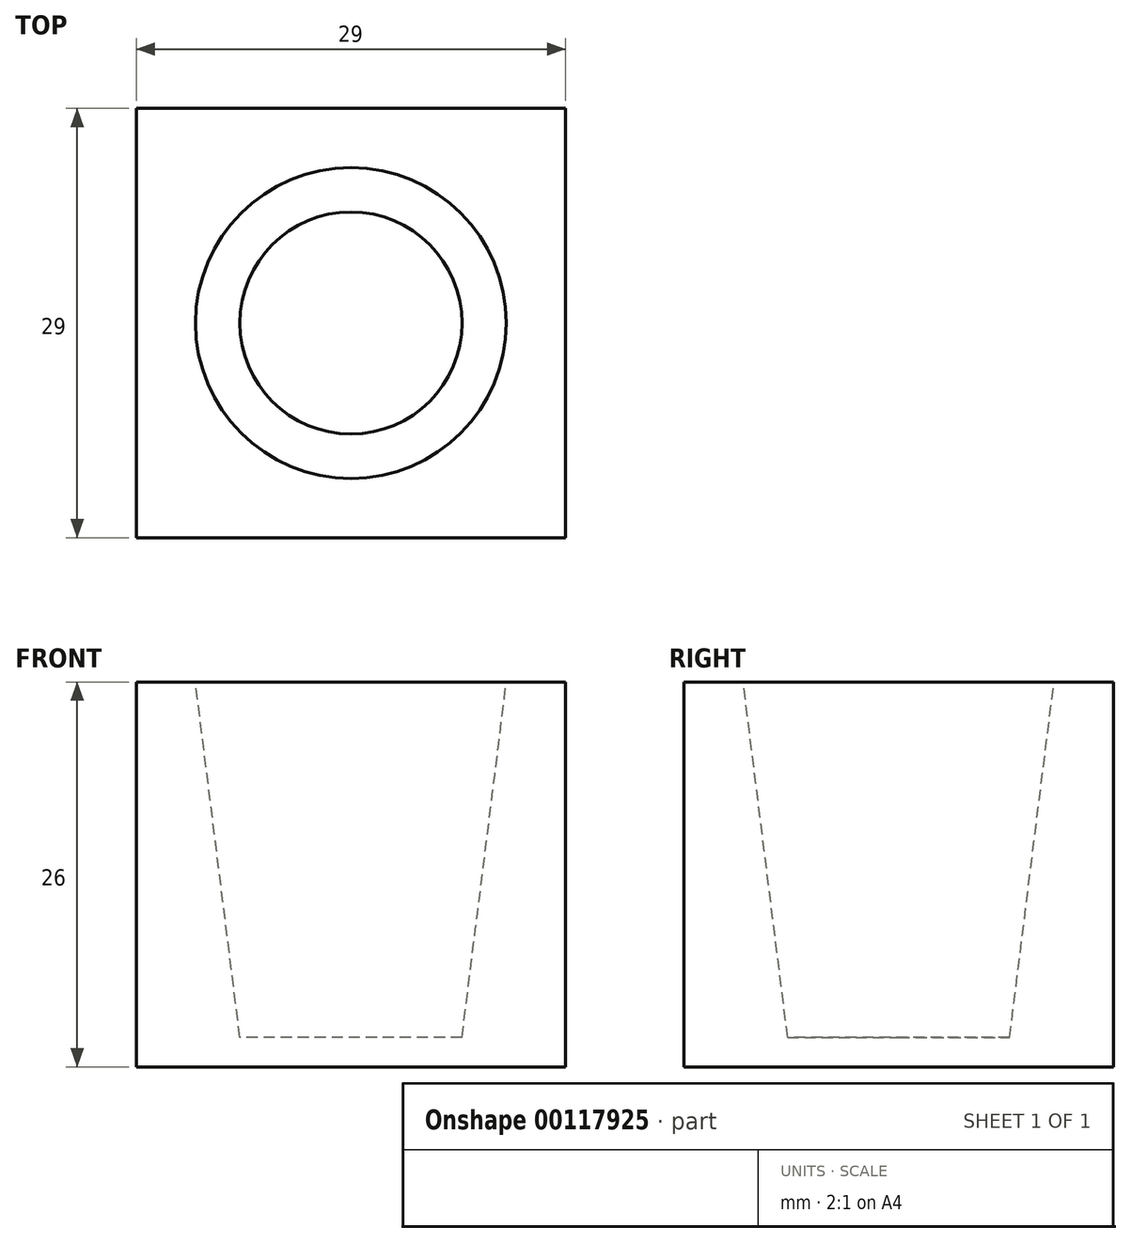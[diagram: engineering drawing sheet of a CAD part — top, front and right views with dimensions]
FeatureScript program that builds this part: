
annotation { "Feature Type Name" : "Feature", "Feature Type Description" : "" }
export const myFeature = defineFeature(function(context is Context, id is Id, definition is map)
    precondition{}
    {
        {
            var Q0;
            Q0=qCreatedBy(makeId("Top.planeOp"),FACE);
            var sketch = newSketch(context, id + "F0", { "sketchPlane" : qUnion([Q0])});
            skCircle(sketch, "E0", {"center": v(0, 0) * mm, "radius": 7.5 * mm});
            skCircle(sketch, "E1", {"center": v(0, 0) * mm, "radius": 10.5 * mm});
            skLineSegment(sketch, "E2.bottom", {"start": v(14.5, -14.5) * mm, "end": v(-14.5, -14.5) * mm});
            skLineSegment(sketch, "E2.top", {"start": v(14.5, 14.5) * mm, "end": v(-14.5, 14.5) * mm});
            skLineSegment(sketch, "E2.left", {"start": v(14.5, -14.5) * mm, "end": v(14.5, 14.5) * mm});
            skLineSegment(sketch, "E2.right", {"start": v(-14.5, -14.5) * mm, "end": v(-14.5, 14.5) * mm});
            skSolve(sketch);
        }
        {
            var Q0;
            Q0=qCreatedBy(makeId("Top.planeOp"),FACE);
            cPlane(context, id + "F1", {"entities" : qUnion([Q0]), "cplaneType" : CPlaneType.OFFSET, "offset" : 24 * mm, "width" : 150 * mm, "height" : 150 * mm});
        }
        {
            var Q0;
            Q0=qCreatedBy(id+"F1.planeOp",FACE);
            var sketch = newSketch(context, id + "F2", { "sketchPlane" : qUnion([Q0])});
            skCircle(sketch, "E3.0", {"center": v(0, 0) * mm, "radius": 10.5 * mm});
            skSolve(sketch);
        }
        {
            var Q0;
            Q0=makeQuery(id+"F0.imprint","IMPRINT",FACE,{"disambiguationData":[TD([[makeQuery(id+"F0.imprint","IMPRINT",EDGE,{"derivedFrom":sQuery(id+"F0.wireOp",EDGE,"E1")}),-1.0]])]});
            var Q1;
            Q1=makeQuery(id+"F0.imprint","IMPRINT",FACE,{"disambiguationData":[TD([[makeQuery(id+"F0.imprint","IMPRINT",EDGE,{"derivedFrom":sQuery(id+"F0.wireOp",EDGE,"E0")}),-1.0]])]});
            var Q2;
            Q2=qCreatedBy(id+"F1.planeOp",FACE);
            extrude(context, id + "F3", {"entities" : qUnion([Q0, Q1]), "endBound" : BoundingType.UP_TO_SURFACE, "endBoundEntityFace" : qUnion([Q2]), "depth" : 25 * mm});
        }
        {
            var Q1;
            Q1=makeQuery(id+"F0.imprint","IMPRINT",FACE,{"disambiguationData":[TD([[makeQuery(id+"F0.imprint","IMPRINT",EDGE,{"derivedFrom":sQuery(id+"F0.wireOp",EDGE,"E0")}),1.0]])]});
            var Q2;
            Q2=makeQuery(id+"F2.imprint","IMPRINT",FACE,{"disambiguationData":[TD([[makeQuery(id+"F2.imprint","IMPRINT",EDGE,{"derivedFrom":sQuery(id+"F2.wireOp",EDGE,"E3.0")}),1.0]])]});
            var Q3;
            Q3=sQuery(id+"F2.wireOp",EDGE,"E3.0");
            var Q4;
            Q4=sQuery(id+"F0.wireOp",EDGE,"E0");
            loft(context, id + "F4", {"operationType" : NewBodyOperationType.REMOVE, "sheetProfilesArray" : [{ "sheetProfileEntities" : qUnion([Q1]) }, { "sheetProfileEntities" : qUnion([Q2]) }], "wireProfilesArray" : [{ "wireProfileEntities" : qUnion([Q3]) }, { "wireProfileEntities" : qUnion([Q4]) }]});
        }
        {
            var Q0;
            Q0=makeQuery(id+"F0.imprint","IMPRINT",FACE,{"disambiguationData":[TD([[makeQuery(id+"F0.imprint","IMPRINT",EDGE,{"derivedFrom":sQuery(id+"F0.wireOp",EDGE,"E1")}),-1.0]])]});
            var Q1;
            Q1=makeQuery(id+"F0.imprint","IMPRINT",FACE,{"disambiguationData":[TD([[makeQuery(id+"F0.imprint","IMPRINT",EDGE,{"derivedFrom":sQuery(id+"F0.wireOp",EDGE,"E0")}),-1.0]])]});
            extrude(context, id + "F5", {"entities" : qUnion([Q0, Q1]), "operationType" : NewBodyOperationType.ADD, "oppositeDirection" : true, "depth" : 1 * mm});
        }
        {
            var Q0;
            Q0=makeQuery(id+"F0.imprint","IMPRINT",FACE,{"disambiguationData":[TD([[makeQuery(id+"F0.imprint","IMPRINT",EDGE,{"derivedFrom":sQuery(id+"F0.wireOp",EDGE,"E1")}),-1.0]])]});
            var Q1;
            Q1=makeQuery(id+"F0.imprint","IMPRINT",FACE,{"disambiguationData":[TD([[makeQuery(id+"F0.imprint","IMPRINT",EDGE,{"derivedFrom":sQuery(id+"F0.wireOp",EDGE,"E0")}),1.0]])]});
            var Q2;
            Q2=makeQuery(id+"F0.imprint","IMPRINT",FACE,{"disambiguationData":[TD([[makeQuery(id+"F0.imprint","IMPRINT",EDGE,{"derivedFrom":sQuery(id+"F0.wireOp",EDGE,"E0")}),-1.0]])]});
            extrude(context, id + "F6", {"entities" : qUnion([Q0, Q1, Q2]), "operationType" : NewBodyOperationType.ADD, "oppositeDirection" : true, "depth" : 2 * mm});
        }
    });
